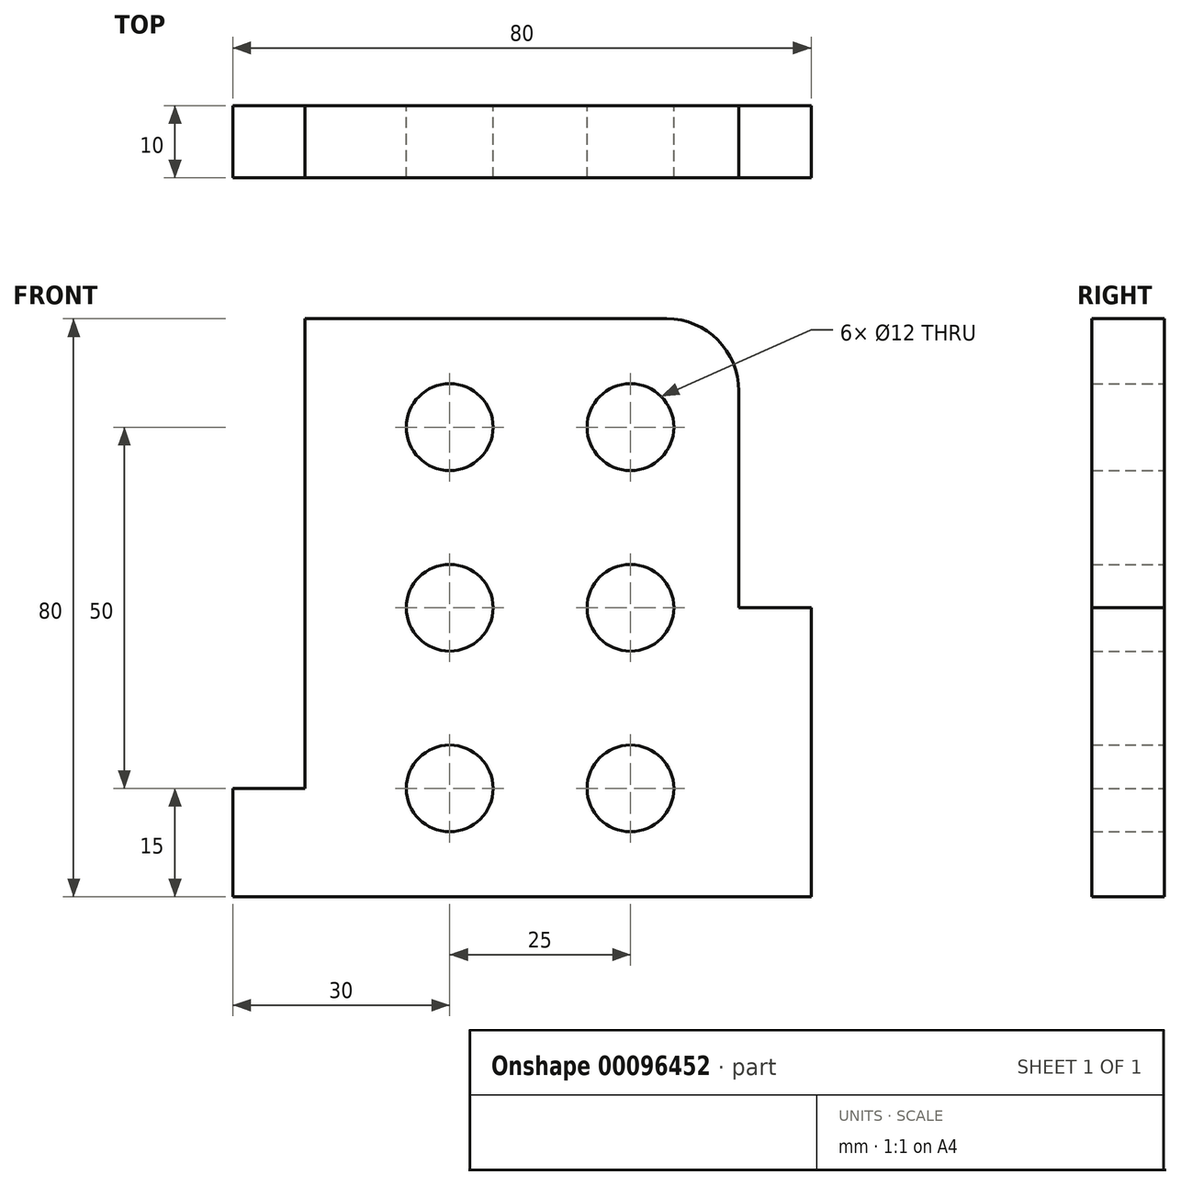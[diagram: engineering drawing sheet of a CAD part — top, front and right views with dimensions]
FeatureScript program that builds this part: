
annotation { "Feature Type Name" : "Feature", "Feature Type Description" : "" }
export const myFeature = defineFeature(function(context is Context, id is Id, definition is map)
    precondition{}
    {
        {
            var Q0;
            Q0=qCreatedBy(makeId("Front.planeOp"),FACE);
            var sketch = newSketch(context, id + "F0", { "sketchPlane" : qUnion([Q0])});
            skLineSegment(sketch, "E0", {"start": v(0, 0) * mm, "end": v(80, 0) * mm});
            skLineSegment(sketch, "E1", {"start": v(80, 0) * mm, "end": v(80, 40) * mm});
            skLineSegment(sketch, "E2", {"start": v(80, 40) * mm, "end": v(70, 40) * mm});
            skLineSegment(sketch, "E3", {"start": v(70, 40) * mm, "end": v(70, 70) * mm});
            skLineSegment(sketch, "E4", {"start": v(60, 80) * mm, "end": v(10, 80) * mm});
            skLineSegment(sketch, "E5", {"start": v(10, 80) * mm, "end": v(10, 15) * mm});
            skLineSegment(sketch, "E6", {"start": v(10, 15) * mm, "end": v(0, 15) * mm});
            skLineSegment(sketch, "E7", {"start": v(0, 15) * mm, "end": v(0, 0) * mm});
            skLineSegment(sketch, "E8", {"start": v(10, 15) * mm, "end": v(80, 15) * mm, "construction": true});
            skLineSegment(sketch, "E9", {"start": v(70, 40) * mm, "end": v(10, 40) * mm, "construction": true});
            skPoint(sketch, "E10.visualSharp", {"position": v(70, 80) * mm});
            skArc(sketch, "E10.filletArc", {"start": v(70, 70) * mm, "mid": v(67.07, 77.07) * mm, "end": v(60, 80) * mm});
            skCircle(sketch, "E11", {"center": v(30, 15) * mm, "radius": 6 * mm});
            skCircle(sketch, "E12", {"center": v(55, 15) * mm, "radius": 6 * mm});
            skCircle(sketch, "E13", {"center": v(30, 40) * mm, "radius": 6 * mm});
            skCircle(sketch, "E14", {"center": v(55, 40) * mm, "radius": 6 * mm});
            skLineSegment(sketch, "E15", {"start": v(10, 65) * mm, "end": v(70, 65) * mm, "construction": true});
            skCircle(sketch, "E16", {"center": v(30, 65) * mm, "radius": 6 * mm});
            skCircle(sketch, "E17", {"center": v(55, 65) * mm, "radius": 6 * mm});
            skLineSegment(sketch, "E18", {"start": v(30, 65) * mm, "end": v(30, 0) * mm, "construction": true});
            skLineSegment(sketch, "E19", {"start": v(55, 65) * mm, "end": v(55, 0) * mm, "construction": true});
            skSolve(sketch);
        }
        {
            var Q0;
            Q0=makeQuery(id+"F0.imprint","IMPRINT",FACE,{"disambiguationData":[TD([[makeQuery(id+"F0.imprint","IMPRINT",EDGE,{"derivedFrom":sQuery(id+"F0.wireOp",EDGE,"E0")}),1.0]])]});
            extrude(context, id + "F1", {"entities" : qUnion([Q0]), "depth" : 10 * mm});
        }
    });
